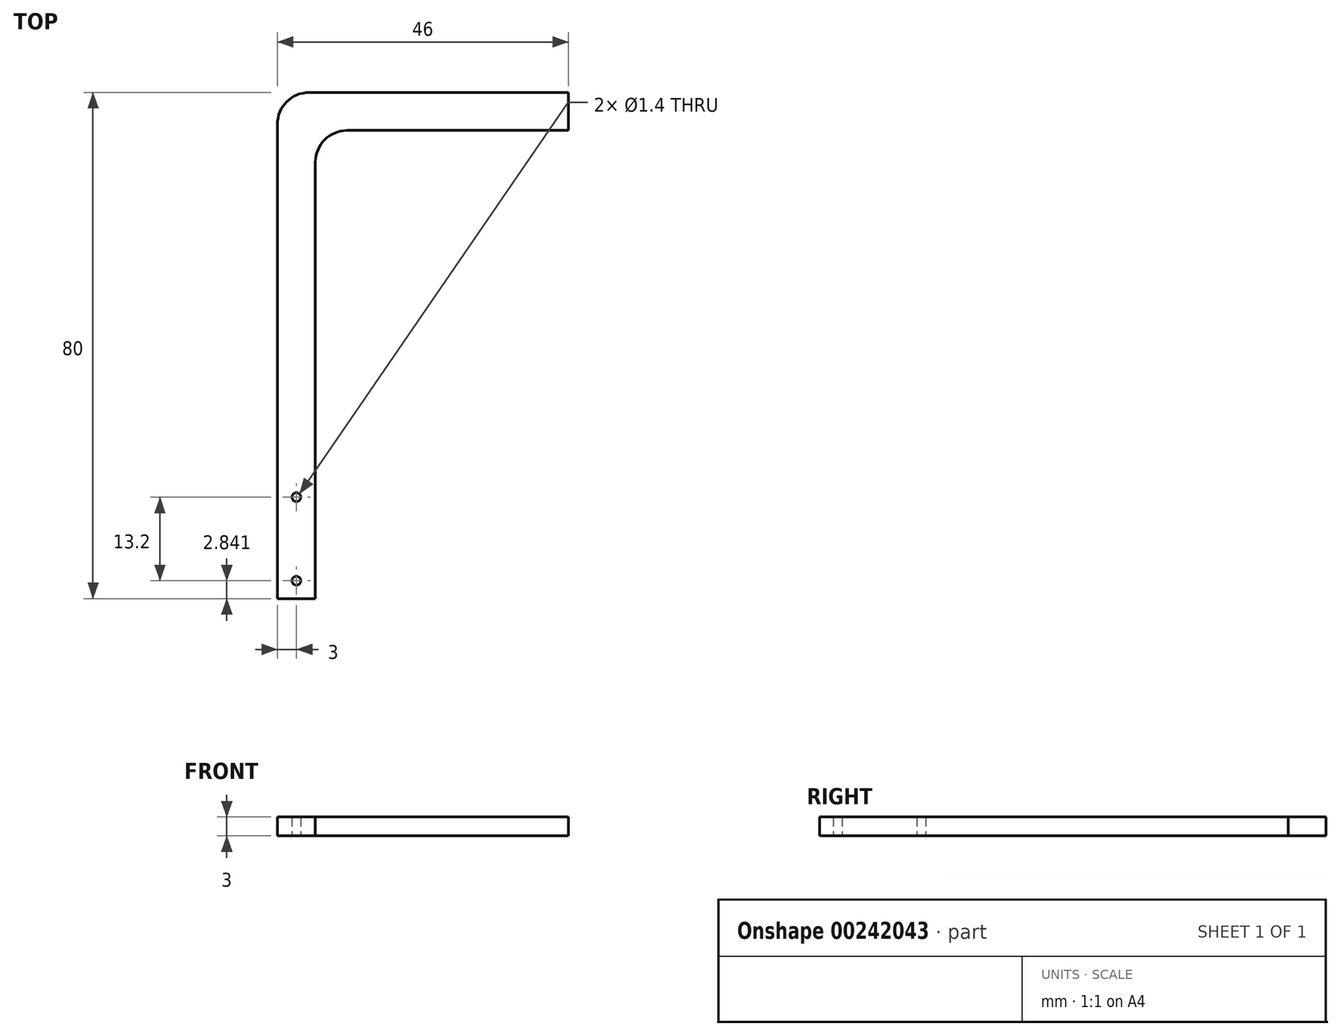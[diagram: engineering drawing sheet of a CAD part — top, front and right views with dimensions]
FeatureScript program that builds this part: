
annotation { "Feature Type Name" : "Feature", "Feature Type Description" : "" }
export const myFeature = defineFeature(function(context is Context, id is Id, definition is map)
    precondition{}
    {
        {
            var Q0;
            Q0=qCreatedBy(makeId("Top.planeOp"),FACE);
            var sketch = newSketch(context, id + "F0", { "sketchPlane" : qUnion([Q0])});
            skLineSegment(sketch, "E0.bottom", {"start": v(0, 0) * mm, "end": v(6, 0) * mm});
            skLineSegment(sketch, "E0.top", {"start": v(5, 80) * mm, "end": v(6, 80) * mm});
            skLineSegment(sketch, "E0.left", {"start": v(0, 0) * mm, "end": v(0, 75) * mm});
            skLineSegment(sketch, "E0.right", {"start": v(6, 0) * mm, "end": v(6, 69) * mm});
            skLineSegment(sketch, "E1.bottom", {"start": v(6, 80) * mm, "end": v(46, 80) * mm});
            skLineSegment(sketch, "E1.top", {"start": v(19.4, 74) * mm, "end": v(46, 74) * mm});
            skLineSegment(sketch, "E1.right", {"start": v(46, 80) * mm, "end": v(46, 74) * mm});
            skLineSegment(sketch, "E2", {"start": v(19.4, 74) * mm, "end": v(11, 74) * mm});
            skCircle(sketch, "E3", {"center": v(3, 2.84) * mm, "radius": 0.7 * mm});
            skPoint(sketch, "E3.centerSnap0", {"position": v(3, 0) * mm});
            skCircle(sketch, "E4.0.1.0", {"center": v(3, 16.04) * mm, "radius": 0.7 * mm});
            skLineSegment(sketch, "E4.direction1", {"start": v(3, 2.84) * mm, "end": v(28, 2.84) * mm, "construction": true});
            skLineSegment(sketch, "E4.direction2", {"start": v(3, 2.84) * mm, "end": v(3, 16.04) * mm, "construction": true});
            skPoint(sketch, "E5.visualSharp", {"position": v(6, 74) * mm});
            skArc(sketch, "E5.filletArc", {"start": v(11, 74) * mm, "mid": v(7.46, 72.54) * mm, "end": v(6, 69) * mm});
            skPoint(sketch, "E6.visualSharp", {"position": v(0, 80) * mm});
            skArc(sketch, "E6.filletArc", {"start": v(5, 80) * mm, "mid": v(1.46, 78.54) * mm, "end": v(0, 75) * mm});
            skSolve(sketch);
        }
        {
            var Q0;
            Q0 = qSketchRegion(id + "F0", true);
            extrude(context, id + "F1", {"entities" : qUnion([Q0]), "depth" : 3 * mm});
        }
    });
